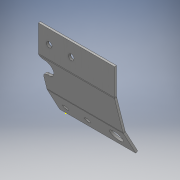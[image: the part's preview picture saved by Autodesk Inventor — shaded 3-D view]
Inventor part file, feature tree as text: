
AUTODESK INVENTOR PART (.ipt)
format: ipt  version: 2018 (Build 220112000, 112)  size: 280,064 bytes
history: native  units: mm
features: other x8, sketch x6, sheet_metal_op x3, hole x3, reference x2, plane x1, fillet x1, projected_geometry x1
ambient origin geometry x8: Origin, YZ Plane, XZ Plane, XY Plane, X Axis, Y Axis, Z Axis, Center Point
bodies: Body1 (feature_tree)
feature tree (25):
  other  "model.ipt"
  plane  "Work Plane1"
  sketch  "Sketch2"  dims[d7=10.0mm d9=5.0mm]
  sheet_metal_op  "Contour Flange1"
  hole  "Hole1"  [1 undecoded]
  hole  "Hole7"  [1 undecoded]
  hole  "Hole8"  [1 undecoded]
  sketch  "Sketch11"  dims[d16=5.0mm]
  fillet  "Fillet1"  Radius=180.0mm
  other  "Plate3"
  sheet_metal_op  "Bend2"
  sheet_metal_op  "Corner1"
  sketch  "Sketch8"  dims[d10=5.0mm d11=2.5mm]
  sketch  "Sketch9"  dims[d12=10.0mm d13=6.25mm d14=180.0mm]
  sketch  "Sketch10"  dims[d15=6.25mm]
  reference  "Reference1"
  reference  "Reference2"
  sketch  "Sketch12"  dims[d17=20.0mm d18=5.0mm d19=6.25mm d20=39.0mm d21=39.0mm d22=13.0mm d23=6.0mm d24=4.0mm d25=2.0mm d26=90.0deg d27=5.0mm d28=20.594885mm d74=62.052154mm d75=25.526077mm d76=26.0mm d77=52.0mm d78=81.718239mm d79=40.85912mm d80=26.0mm d81=52.0mm d82=13.0mm d83=6.0mm d84=4.0mm d85=2.0mm d86=90.0deg d87=5.0mm d88=20.594885mm d89=63.10912mm d90=31.55456mm d91=26.0mm d92=52.0mm d93=13.0mm d94=6.0mm d95=4.0mm d96=2.0mm d97=90.0deg d98=5.0mm d99=20.594885mm d100=20.0mm d101=20.0mm d102=302.737mm d103=30.0mm d104=302.737mm d105=5.0mm d106=0.0mm d107=18.5mm d108=30.0mm d109=62.052154mm d110=31.026077mm d111=31.026077mm d112=5.0mm d113=0.0mm d114=10.0mm d29=1.0mm d30=1.0mm]
  projected_geometry  "Projected Loop1"
  other  "Cut1"
  other  "Cut2"
  parser-record x1  (decoder bookkeeping rows leaked as tree rows — omitted from the tree; the rows remain in map.json)
  other  "modul.iam"
  other  "vange:1"
  other  "Definition1"
note: 3 required parameter values undecoded (feature->parameter linkage not recoverable at this tier; creation-order binding heuristic only, values carry confidence <= 0.55)
note: 1 file-system path scrubbed to <path> (originals preserved in map.json)
